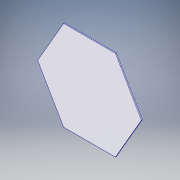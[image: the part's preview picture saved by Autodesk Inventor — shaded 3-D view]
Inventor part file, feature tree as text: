
AUTODESK INVENTOR PART (.ipt)
format: ipt  version: 2019 (Build 230136000, 136)  size: 95,744 bytes
history: native  units: mm
features: extrude x1, sketch x1
ambient origin geometry x8: Origin, YZ Plane, XZ Plane, XY Plane, X Axis, Y Axis, Z Axis, Center Point
bodies: Solid1 (feature_tree)
feature tree (2):
  extrude  "Extrusion1"  Depth=2.0mm TaperAngle=0.0deg
  sketch  "Sketch1"  dims[d0=186.0mm d1=2.0mm d2=0.0mm]
